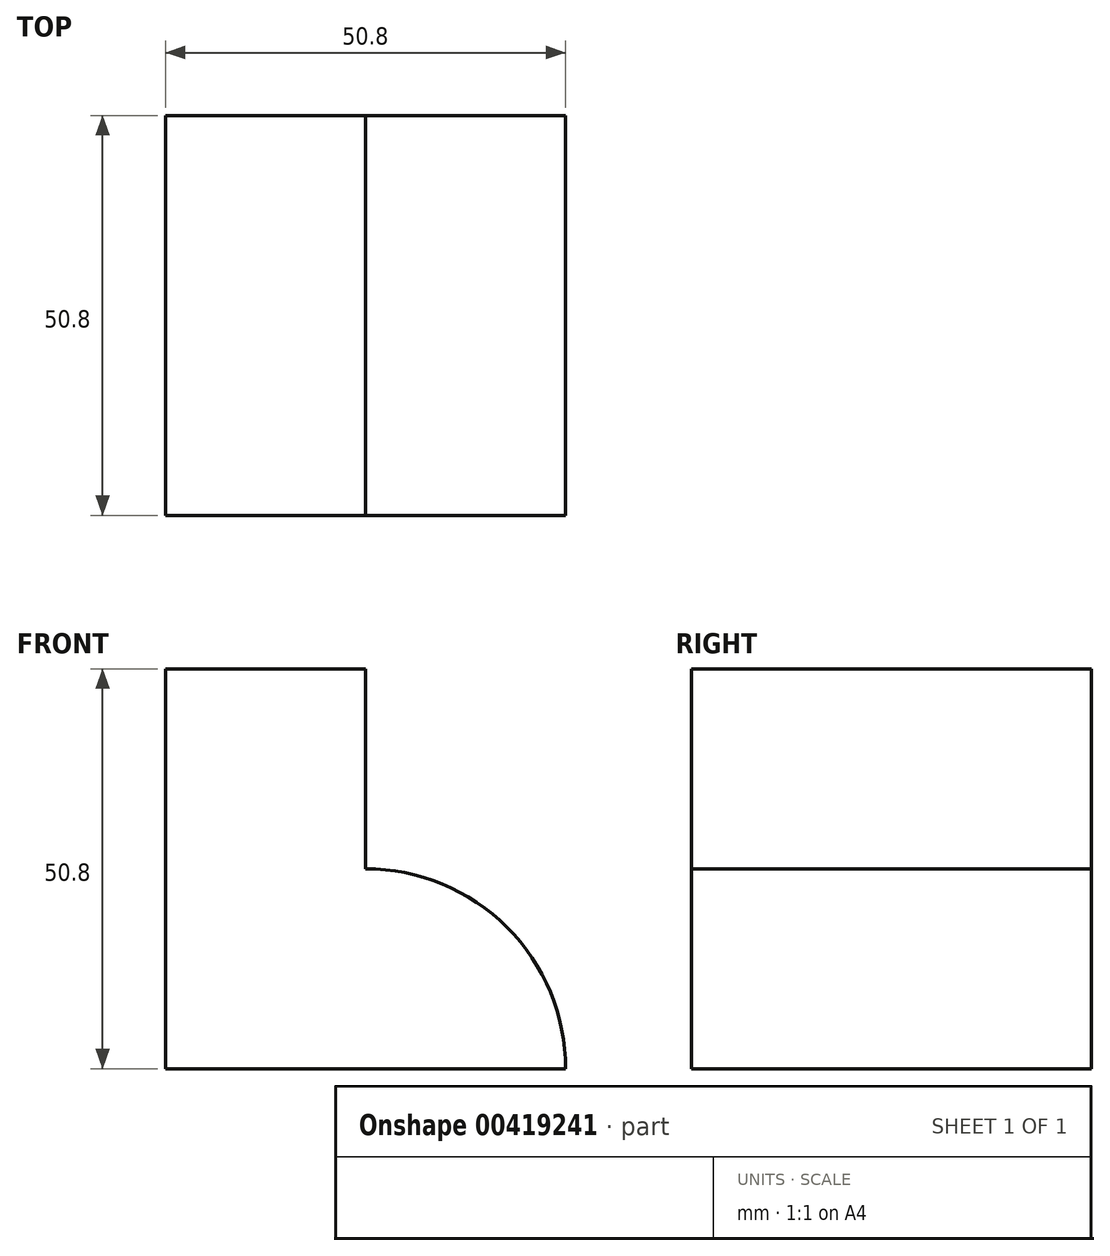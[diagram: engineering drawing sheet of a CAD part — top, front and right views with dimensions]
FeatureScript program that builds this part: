
annotation { "Feature Type Name" : "Feature", "Feature Type Description" : "" }
export const myFeature = defineFeature(function(context is Context, id is Id, definition is map)
    precondition{}
    {
        {
            var Q0;
            Q0=qCreatedBy(makeId("Front.planeOp"),FACE);
            var sketch = newSketch(context, id + "F0", { "sketchPlane" : qUnion([Q0])});
            skLineSegment(sketch, "E0", {"start": v(0, 0) * mm, "end": v(0, 50.8) * mm});
            skLineSegment(sketch, "E1", {"start": v(0, 50.8) * mm, "end": v(25.4, 50.8) * mm});
            skLineSegment(sketch, "E2", {"start": v(25.4, 50.8) * mm, "end": v(25.4, 25.4) * mm});
            skLineSegment(sketch, "E3", {"start": v(0, 0) * mm, "end": v(50.8, 0) * mm});
            skArc(sketch, "E4", {"start": v(50.8, 0) * mm, "mid": v(43.37, 17.97) * mm, "end": v(25.4, 25.4) * mm});
            skSolve(sketch);
        }
        {
            var Q0;
            Q0 = qSketchRegion(id + "F0", true);
            extrude(context, id + "F1", {"entities" : qUnion([Q0]), "depth" : 50.8 * mm});
        }
    });
